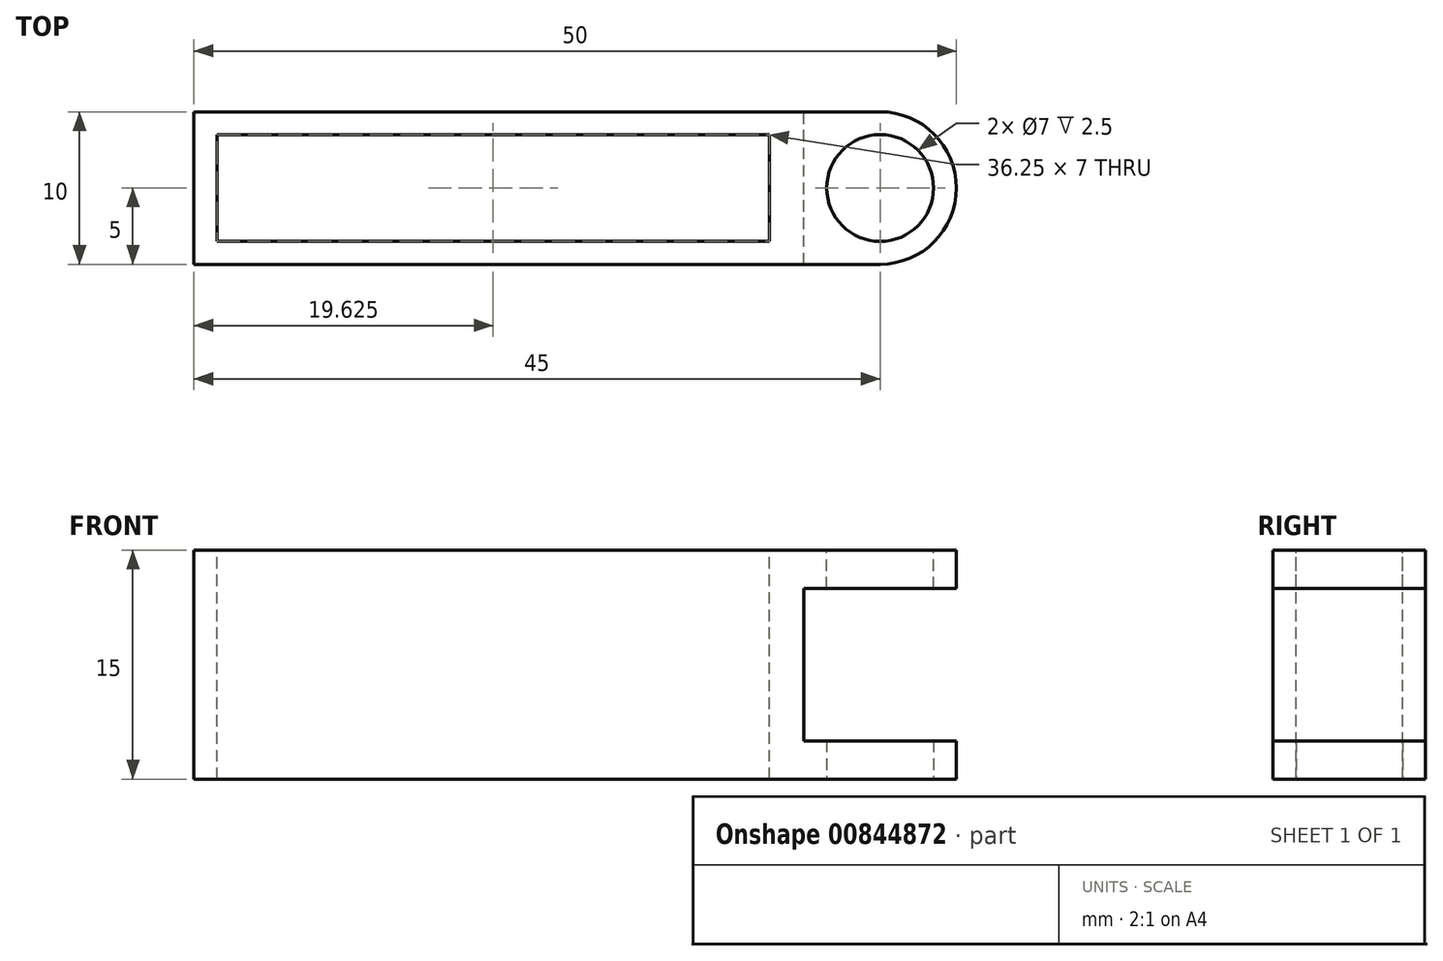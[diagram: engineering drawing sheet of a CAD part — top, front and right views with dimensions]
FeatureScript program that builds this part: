
annotation { "Feature Type Name" : "Feature", "Feature Type Description" : "" }
export const myFeature = defineFeature(function(context is Context, id is Id, definition is map)
    precondition{}
    {
        {
            var Q0;
            Q0=qCreatedBy(makeId("Top.planeOp"),FACE);
            var sketch = newSketch(context, id + "F0", { "sketchPlane" : qUnion([Q0])});
            skLineSegment(sketch, "E0.bottom", {"start": v(0, 0) * mm, "end": v(40, 0) * mm});
            skLineSegment(sketch, "E0.top", {"start": v(0, 10) * mm, "end": v(40, 10) * mm});
            skLineSegment(sketch, "E0.left", {"start": v(0, 0) * mm, "end": v(0, 10) * mm});
            skLineSegment(sketch, "E0.right", {"start": v(40, 0) * mm, "end": v(40, 10) * mm});
            skSolve(sketch);
        }
        {
            var Q0;
            Q0 = qSketchRegion(id + "F0", true);
            extrude(context, id + "F1", {"entities" : qUnion([Q0]), "depth" : 5 * mm, "offsetDistance" : 25.4 * mm});
        }
        {
            var Q0;
            Q0=makeQuery(id+"F1.opExtrude","CAP_FACE",FACE,{"disambiguationData":[OSD([sQuery(id+"F0.wireOp",EDGE,"E0.bottom"),sQuery(id+"F0.wireOp",EDGE,"E0.top"),sQuery(id+"F0.wireOp",EDGE,"E0.left"),sQuery(id+"F0.wireOp",EDGE,"E0.right")])],"isStart":false});
            var sketch = newSketch(context, id + "F2", { "sketchPlane" : qUnion([Q0])});
            skArc(sketch, "E1", {"start": v(45, 0) * mm, "mid": v(50, 5) * mm, "end": v(45, 10) * mm});
            skLineSegment(sketch, "E2", {"start": v(45, 10) * mm, "end": v(40, 10) * mm});
            skLineSegment(sketch, "E3", {"start": v(45, 0) * mm, "end": v(40, 0) * mm});
            skLineSegment(sketch, "E4.0", {"start": v(0, 10) * mm, "end": v(40, 10) * mm});
            skLineSegment(sketch, "E5.0", {"start": v(0, 0) * mm, "end": v(40, 0) * mm});
            skLineSegment(sketch, "E6.0", {"start": v(0, 0) * mm, "end": v(0, 10) * mm});
            skSolve(sketch);
        }
        {
            var Q0;
            Q0 = qSketchRegion(id + "F2", true);
            extrude(context, id + "F3", {"entities" : qUnion([Q0]), "operationType" : NewBodyOperationType.ADD, "depth" : 2.5 * mm, "offsetDistance" : 25.4 * mm});
        }
        {
            var Q0;
            Q0=makeQuery(id+"F3.opExtrude","CAP_FACE",FACE,{"disambiguationData":[OSD([sQuery(id+"F2.wireOp",EDGE,"E1"),sQuery(id+"F2.wireOp",EDGE,"E2"),sQuery(id+"F2.wireOp",EDGE,"E3"),sQuery(id+"F2.wireOp",EDGE,"E4.0"),sQuery(id+"F2.wireOp",EDGE,"E5.0"),sQuery(id+"F2.wireOp",EDGE,"E6.0")])],"isStart":false});
            var sketch = newSketch(context, id + "F4", { "sketchPlane" : qUnion([Q0])});
            skCircle(sketch, "E7", {"center": v(45, 5) * mm, "radius": 3.5 * mm});
            skSolve(sketch);
        }
        {
            var Q0;
            Q0 = qSketchRegion(id + "F4", true);
            extrude(context, id + "F5", {"entities" : qUnion([Q0]), "operationType" : NewBodyOperationType.REMOVE, "endBound" : BoundingType.THROUGH_ALL, "oppositeDirection" : true, "depth" : 25.4 * mm, "offsetDistance" : 25.4 * mm});
        }
        {
            var Q0;
            Q0=makeQuery(id+"F3.opExtrude","CAP_FACE",FACE,{"disambiguationData":[OSD([sQuery(id+"F2.wireOp",EDGE,"E1"),sQuery(id+"F2.wireOp",EDGE,"E2"),sQuery(id+"F2.wireOp",EDGE,"E3"),sQuery(id+"F2.wireOp",EDGE,"E4.0"),sQuery(id+"F2.wireOp",EDGE,"E5.0"),sQuery(id+"F2.wireOp",EDGE,"E6.0")])],"isStart":false});
            var sketch = newSketch(context, id + "F6", { "sketchPlane" : qUnion([Q0])});
            skLineSegment(sketch, "E8.0", {"start": v(37.75, 1.5) * mm, "end": v(1.5, 1.5) * mm});
            skLineSegment(sketch, "E8.1", {"start": v(1.5, 1.5) * mm, "end": v(1.5, 8.5) * mm});
            skLineSegment(sketch, "E8.2", {"start": v(37.75, 8.5) * mm, "end": v(1.5, 8.5) * mm});
            skLineSegment(sketch, "E9", {"start": v(37.75, 8.5) * mm, "end": v(37.75, 1.5) * mm});
            skSolve(sketch);
        }
        {
            var Q0;
            Q0 = qSketchRegion(id + "F6", true);
            extrude(context, id + "F7", {"entities" : qUnion([Q0]), "operationType" : NewBodyOperationType.REMOVE, "endBound" : BoundingType.THROUGH_ALL, "oppositeDirection" : true, "depth" : 25.4 * mm, "offsetDistance" : 25.4 * mm});
        }
        {
            var Q0;
            Q0=makeQuery(id+"F1.opExtrude","SWEPT_BODY",BODY,{"disambiguationData":[OSD([sQuery(id+"F0.wireOp",EDGE,"E0.bottom"),sQuery(id+"F0.wireOp",EDGE,"E0.top"),sQuery(id+"F0.wireOp",EDGE,"E0.left"),sQuery(id+"F0.wireOp",EDGE,"E0.right")])]});
            var Q1;
            Q1=qCreatedBy(makeId("Top.planeOp"),FACE);
            mirror(context, id + "F8", {"operationType" : NewBodyOperationType.ADD, "entities" : qUnion([Q0]), "mirrorPlane" : qUnion([Q1])});
        }
    });
